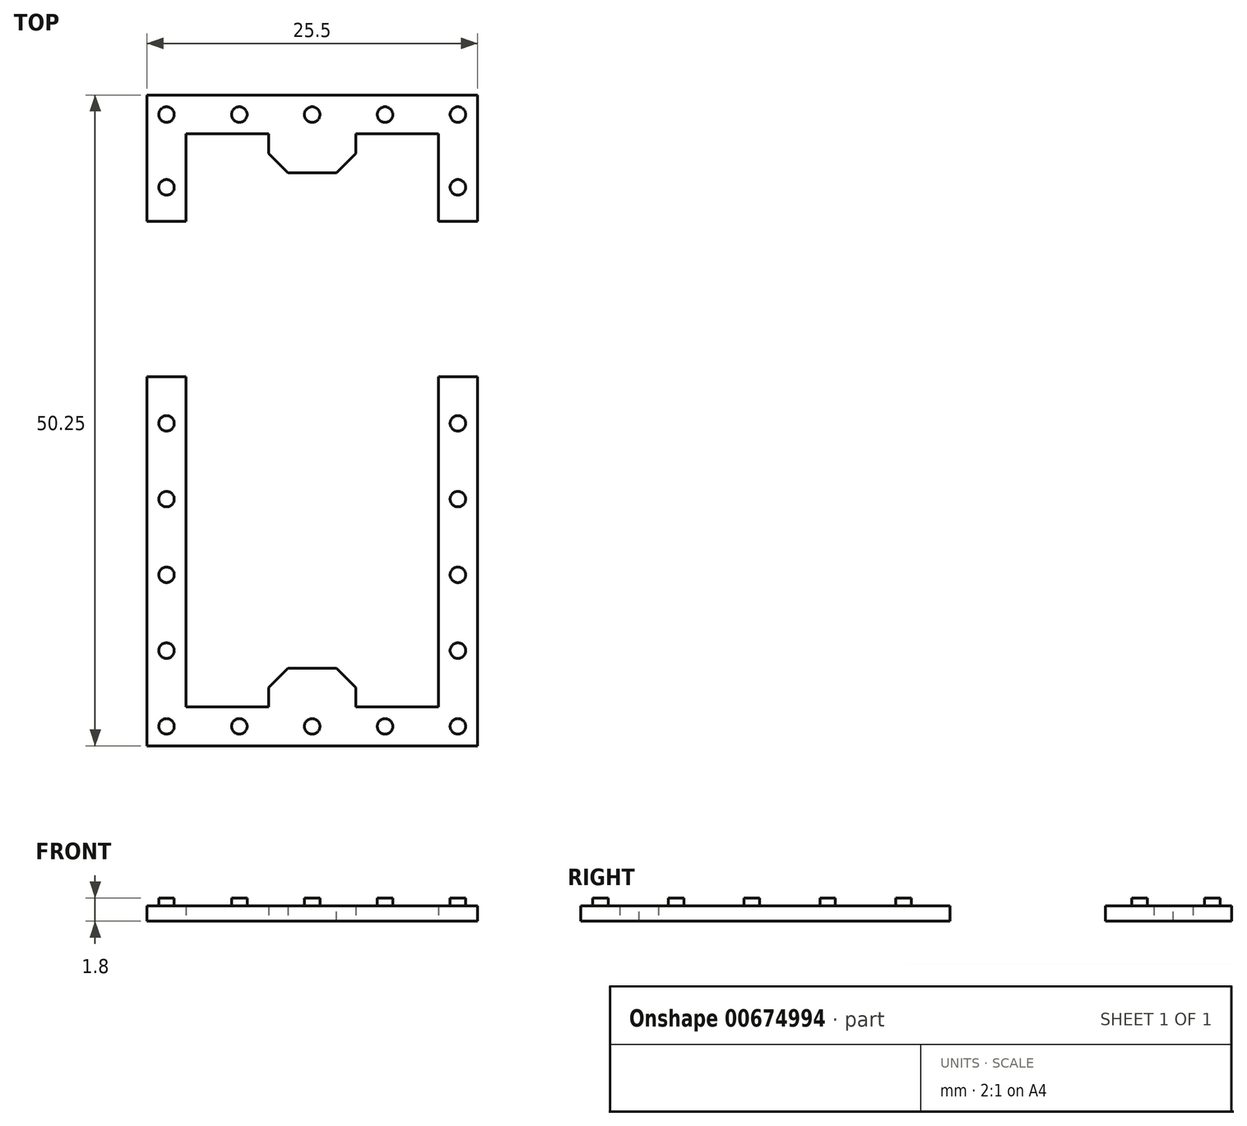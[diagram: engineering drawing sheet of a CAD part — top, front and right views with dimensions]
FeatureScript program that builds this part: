
annotation { "Feature Type Name" : "Feature", "Feature Type Description" : "" }
export const myFeature = defineFeature(function(context is Context, id is Id, definition is map)
    precondition{}
    {
        {
            assignVariable(context, id + "F0", {"name" : "Faktor", "anyValue" : 1.5});
        }
        {
            var Q0;
            Q0=qCreatedBy(makeId("Top.planeOp"),FACE);
            var sketch = newSketch(context, id + "F1", { "sketchPlane" : qUnion([Q0])});
            skLineSegment(sketch, "E0.bottom", {"start": v(-12.75, 15.75) * mm, "end": v(12.75, 15.75) * mm});
            skLineSegment(sketch, "E0.top", {"start": v(-12.75, -34.5) * mm, "end": v(12.75, -34.5) * mm});
            skLineSegment(sketch, "E0.left", {"start": v(-12.75, 15.75) * mm, "end": v(-12.75, 6) * mm});
            skLineSegment(sketch, "E0.right", {"start": v(12.75, 15.75) * mm, "end": v(12.75, 6) * mm});
            skLineSegment(sketch, "E1.bottom", {"start": v(-9.75, 12.75) * mm, "end": v(-3.38, 12.75) * mm});
            skLineSegment(sketch, "E1.top", {"start": v(-9.75, -31.5) * mm, "end": v(-3.37, -31.5) * mm});
            skLineSegment(sketch, "E1.left", {"start": v(-9.75, 12.75) * mm, "end": v(-9.75, 6) * mm});
            skLineSegment(sketch, "E1.right", {"start": v(9.75, 12.75) * mm, "end": v(9.75, 6) * mm});
            skLineSegment(sketch, "E2", {"start": v(-12.75, 6) * mm, "end": v(-9.75, 6) * mm});
            skLineSegment(sketch, "E3", {"start": v(-12.75, -6) * mm, "end": v(-9.75, -6) * mm});
            skLineSegment(sketch, "E4.trimOffspring", {"start": v(-9.75, -6) * mm, "end": v(-9.75, -31.5) * mm});
            skLineSegment(sketch, "E5.trimOffspring", {"start": v(-12.75, -6) * mm, "end": v(-12.75, -34.5) * mm});
            skLineSegment(sketch, "E6.trimOffspring", {"start": v(9.75, -6) * mm, "end": v(9.75, -31.5) * mm});
            skLineSegment(sketch, "E7.trimOffspring", {"start": v(12.75, -6) * mm, "end": v(12.75, -34.5) * mm});
            skLineSegment(sketch, "E8.trimOffspring", {"start": v(9.75, 6) * mm, "end": v(12.75, 6) * mm});
            skLineSegment(sketch, "E9.trimOffspring", {"start": v(9.75, -6) * mm, "end": v(12.75, -6) * mm});
            skLineSegment(sketch, "E10.top", {"start": v(-3.37, -28.5) * mm, "end": v(3.37, -28.5) * mm});
            skLineSegment(sketch, "E10.left", {"start": v(-3.37, -31.5) * mm, "end": v(-3.37, -28.5) * mm});
            skLineSegment(sketch, "E10.right", {"start": v(3.37, -31.5) * mm, "end": v(3.37, -28.5) * mm});
            skLineSegment(sketch, "E11.trimOffspring", {"start": v(3.37, -31.5) * mm, "end": v(9.75, -31.5) * mm});
            skLineSegment(sketch, "E12", {"start": v(-3.38, 12.75) * mm, "end": v(-3.38, 9.75) * mm});
            skLineSegment(sketch, "E13", {"start": v(-3.38, 9.75) * mm, "end": v(3.38, 9.75) * mm});
            skLineSegment(sketch, "E14", {"start": v(3.38, 9.75) * mm, "end": v(3.38, 12.75) * mm});
            skLineSegment(sketch, "E15.trimOffspring", {"start": v(3.38, 12.75) * mm, "end": v(9.75, 12.75) * mm});
            skSolve(sketch);
        }
        {
            var Q0;
            Q0=qSketchRegion(id+"F1",true);
            extrude(context, id + "F2", {"entities" : qUnion([Q0]), "depth" : getVariable(context, 'Faktor') * 0.8 * mm, "offsetDistance" : 25 * mm});
        }
        {
            var Q0;
            Q0=makeQuery(id+"F2.opExtrude","CAP_FACE",FACE,{"disambiguationData":[OSD([sQuery(id+"F1.wireOp",EDGE,"E0.bottom"),sQuery(id+"F1.wireOp",EDGE,"E0.left"),sQuery(id+"F1.wireOp",EDGE,"E0.right"),sQuery(id+"F1.wireOp",EDGE,"E1.bottom"),sQuery(id+"F1.wireOp",EDGE,"E1.left"),sQuery(id+"F1.wireOp",EDGE,"E1.right"),sQuery(id+"F1.wireOp",EDGE,"E2"),sQuery(id+"F1.wireOp",EDGE,"E8.trimOffspring")])],"isStart":false});
            var sketch = newSketch(context, id + "F3", { "sketchPlane" : qUnion([Q0])});
            skCircle(sketch, "E16", {"center": v(-11.25, 14.25) * mm, "radius": 0.6 * mm});
            skLineSegment(sketch, "E17.bottom", {"start": v(-11.25, -33) * mm, "end": v(11.25, -33) * mm, "construction": true});
            skLineSegment(sketch, "E17.top", {"start": v(-11.25, 14.25) * mm, "end": v(11.25, 14.25) * mm, "construction": true});
            skLineSegment(sketch, "E17.left", {"start": v(-11.25, -33) * mm, "end": v(-11.25, 14.25) * mm, "construction": true});
            skLineSegment(sketch, "E17.right", {"start": v(11.25, -33) * mm, "end": v(11.25, 14.25) * mm, "construction": true});
            skCircle(sketch, "E18", {"center": v(-5.63, 14.25) * mm, "radius": 0.6 * mm});
            skCircle(sketch, "E19", {"center": v(0, 14.25) * mm, "radius": 0.6 * mm});
            skCircle(sketch, "E20", {"center": v(5.62, 14.25) * mm, "radius": 0.6 * mm});
            skCircle(sketch, "E21", {"center": v(11.25, 14.25) * mm, "radius": 0.6 * mm});
            skCircle(sketch, "E22", {"center": v(-11.25, 8.62) * mm, "radius": 0.6 * mm});
            skCircle(sketch, "E23", {"center": v(11.25, 8.62) * mm, "radius": 0.6 * mm});
            skCircle(sketch, "E24", {"center": v(0, -33) * mm, "radius": 0.6 * mm});
            skCircle(sketch, "E25", {"center": v(5.63, -33) * mm, "radius": 0.6 * mm});
            skCircle(sketch, "E26", {"center": v(11.25, -33) * mm, "radius": 0.6 * mm});
            skCircle(sketch, "E27", {"center": v(-5.62, -33) * mm, "radius": 0.6 * mm});
            skCircle(sketch, "E28", {"center": v(-11.25, -33) * mm, "radius": 0.6 * mm});
            skCircle(sketch, "E29", {"center": v(-11.25, -27.15) * mm, "radius": 0.6 * mm});
            skCircle(sketch, "E30", {"center": v(-11.25, -21.3) * mm, "radius": 0.6 * mm});
            skCircle(sketch, "E31", {"center": v(-11.25, -15.45) * mm, "radius": 0.6 * mm});
            skCircle(sketch, "E32", {"center": v(-11.25, -9.6) * mm, "radius": 0.6 * mm});
            skCircle(sketch, "E33", {"center": v(11.25, -27.15) * mm, "radius": 0.6 * mm});
            skCircle(sketch, "E34", {"center": v(11.25, -21.3) * mm, "radius": 0.6 * mm});
            skCircle(sketch, "E35", {"center": v(11.25, -15.45) * mm, "radius": 0.6 * mm});
            skCircle(sketch, "E36", {"center": v(11.25, -9.6) * mm, "radius": 0.6 * mm});
            skSolve(sketch);
        }
        {
            var Q0;
            Q0=qSketchRegion(id+"F3",true);
            extrude(context, id + "F4", {"entities" : qUnion([Q0]), "depth" : getVariable(context, 'Faktor') * 0.4 * mm, "offsetDistance" : 25 * mm});
        }
        {
            var Q0;
            Q0=makeQuery(id+"F2.opExtrude","SWEPT_EDGE",EDGE,{"disambiguationData":[OSD([sQuery(id+"F1.wireOp",EDGE,"E12"),sQuery(id+"F1.wireOp",EDGE,"E13")])]});
            var Q1;
            Q1=makeQuery(id+"F2.opExtrude","SWEPT_EDGE",EDGE,{"disambiguationData":[OSD([sQuery(id+"F1.wireOp",EDGE,"E13"),sQuery(id+"F1.wireOp",EDGE,"E14")])]});
            var Q2;
            Q2=makeQuery(id+"F2.opExtrude","SWEPT_EDGE",EDGE,{"disambiguationData":[OSD([sQuery(id+"F1.wireOp",EDGE,"E10.top"),sQuery(id+"F1.wireOp",EDGE,"E10.right")])]});
            var Q3;
            Q3=makeQuery(id+"F2.opExtrude","SWEPT_EDGE",EDGE,{"disambiguationData":[OSD([sQuery(id+"F1.wireOp",EDGE,"E10.top"),sQuery(id+"F1.wireOp",EDGE,"E10.left")])]});
            chamfer(context, id + "F5", {"entities" : qUnion([Q0, Q1, Q2, Q3]), "width" : getVariable(context, 'Faktor') * 1 * mm, "tangentPropagation" : true});
        }
    });
